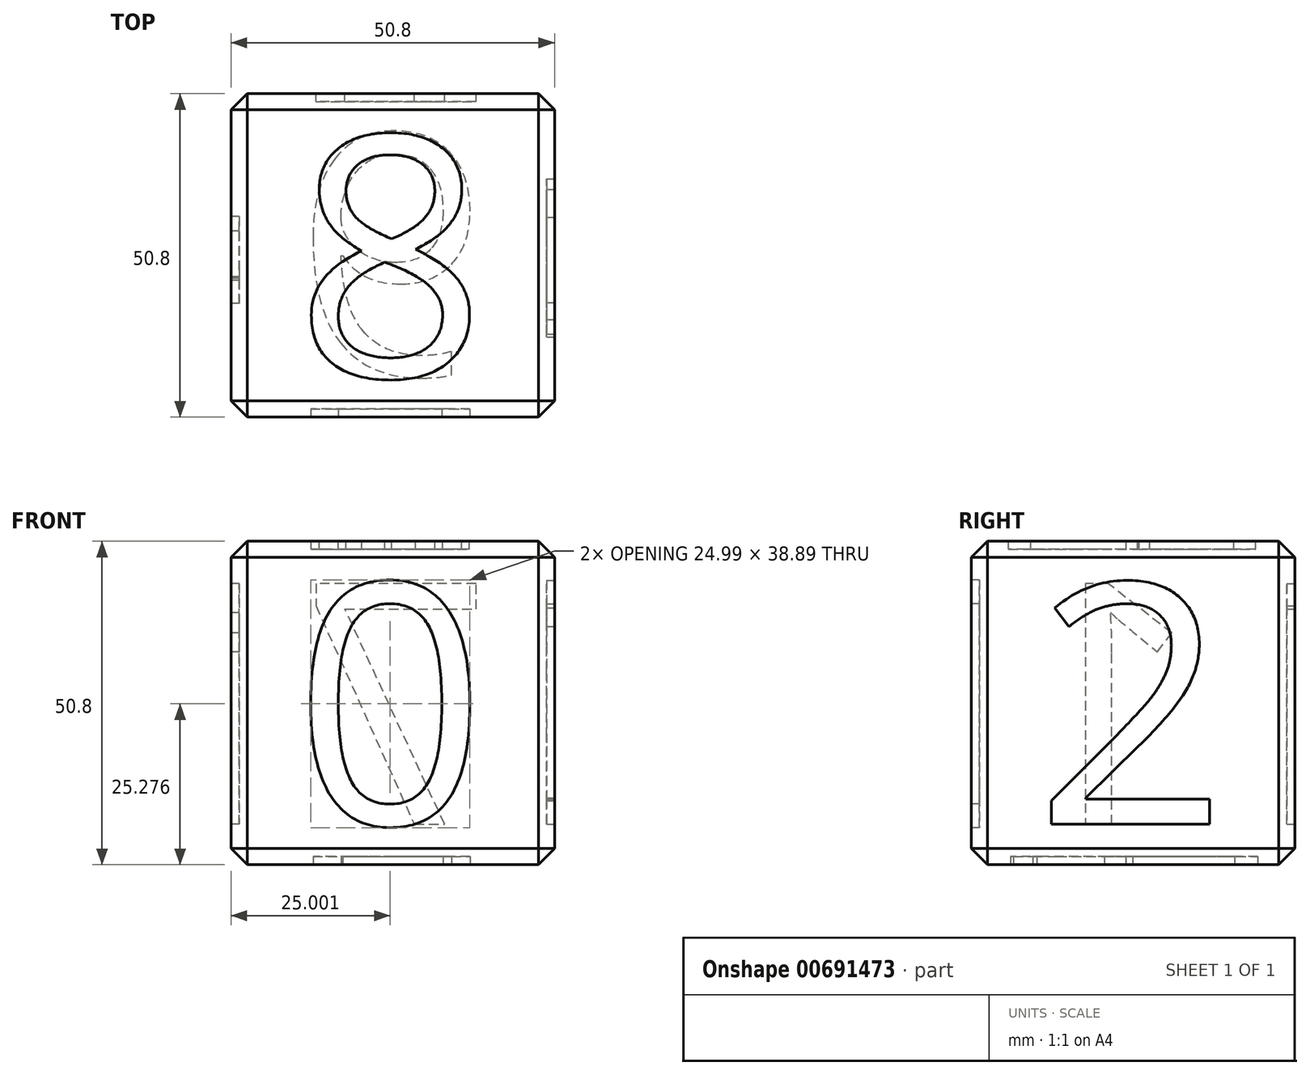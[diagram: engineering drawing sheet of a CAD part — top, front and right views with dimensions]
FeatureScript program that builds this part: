
annotation { "Feature Type Name" : "Feature", "Feature Type Description" : "" }
export const myFeature = defineFeature(function(context is Context, id is Id, definition is map)
    precondition{}
    {
        {
            var Q0;
            Q0=qCreatedBy(makeId("Top.planeOp"),FACE);
            var sketch = newSketch(context, id + "F0", { "sketchPlane" : qUnion([Q0])});
            skLineSegment(sketch, "E0.bottom", {"start": v(25.4, 25.4) * mm, "end": v(-25.4, 25.4) * mm});
            skLineSegment(sketch, "E0.top", {"start": v(25.4, -25.4) * mm, "end": v(-25.4, -25.4) * mm});
            skLineSegment(sketch, "E0.left", {"start": v(25.4, 25.4) * mm, "end": v(25.4, -25.4) * mm});
            skLineSegment(sketch, "E0.right", {"start": v(-25.4, 25.4) * mm, "end": v(-25.4, -25.4) * mm});
            skPoint(sketch, "E0.middle", {"position": v(0, 0) * mm});
            skSolve(sketch);
        }
        {
            var Q0;
            Q0 = qSketchRegion(id + "F0", true);
            extrude(context, id + "F1", {"entities" : qUnion([Q0]), "depth" : 25.4 * mm, "offsetDistance" : 25.4 * mm, "hasSecondDirection" : true, "secondDirectionOppositeDirection" : true, "secondDirectionDepth" : 25.4 * mm});
        }
        {
            var Q0;
            Q0=makeQuery(id+"F1.opExtrude","SWEPT_FACE",FACE,{"disambiguationData":[OSD([sQuery(id+"F0.wireOp",EDGE,"E0.bottom")])]});
            var Q1;
            Q1=makeQuery(id+"F1.opExtrude","CAP_FACE",FACE,{"disambiguationData":[OSD([sQuery(id+"F0.wireOp",EDGE,"E0.bottom"),sQuery(id+"F0.wireOp",EDGE,"E0.top"),sQuery(id+"F0.wireOp",EDGE,"E0.left"),sQuery(id+"F0.wireOp",EDGE,"E0.right")])],"isStart":false});
            var Q2;
            Q2=makeQuery(id+"F1.opExtrude","SWEPT_FACE",FACE,{"disambiguationData":[OSD([sQuery(id+"F0.wireOp",EDGE,"E0.left")])]});
            var Q3;
            Q3=makeQuery(id+"F1.opExtrude","CAP_FACE",FACE,{"disambiguationData":[OSD([sQuery(id+"F0.wireOp",EDGE,"E0.bottom"),sQuery(id+"F0.wireOp",EDGE,"E0.top"),sQuery(id+"F0.wireOp",EDGE,"E0.left"),sQuery(id+"F0.wireOp",EDGE,"E0.right")])],"isStart":true});
            var Q4;
            Q4=makeQuery(id+"F1.opExtrude","SWEPT_FACE",FACE,{"disambiguationData":[OSD([sQuery(id+"F0.wireOp",EDGE,"E0.right")])]});
            var Q5;
            Q5=makeQuery(id+"F1.opExtrude","SWEPT_FACE",FACE,{"disambiguationData":[OSD([sQuery(id+"F0.wireOp",EDGE,"E0.top")])]});
            chamfer(context, id + "F2", {"entities" : qUnion([Q0, Q1, Q2, Q3, Q4, Q5]), "width" : 2.54 * mm, "tangentPropagation" : true});
        }
        {
            var Q0;
            Q0=makeQuery(id+"F1.opExtrude","SWEPT_FACE",FACE,{"disambiguationData":[OSD([sQuery(id+"F0.wireOp",EDGE,"E0.top")])]});
            var sketch = newSketch(context, id + "F3", { "sketchPlane" : qUnion([Q0])});
            skText(sketch, "E1", { "text": "0", "fontName": "OpenSans-Regular.ttf"});
            skLineSegment(sketch, "E2", {"start": v(-29.8, 0) * mm, "end": v(-15.53, 0) * mm, "construction": true});
            const initialGuessF3  = {"E1": [-0.01553, -0.01905, 1, 0, 0.0381]};
            skSetInitialGuess(sketch, initialGuessF3);
            skSolve(sketch);
        }
        {
            var Q0;
            Q0 = qSketchRegion(id + "F3", true);
            extrude(context, id + "F4", {"entities" : qUnion([Q0]), "operationType" : NewBodyOperationType.REMOVE, "oppositeDirection" : true, "depth" : 1.27 * mm, "offsetDistance" : 25.4 * mm});
        }
        {
            var Q0;
            Q0=makeQuery(id+"F1.opExtrude","SWEPT_FACE",FACE,{"disambiguationData":[OSD([sQuery(id+"F0.wireOp",EDGE,"E0.right")])]});
            var sketch = newSketch(context, id + "F5", { "sketchPlane" : qUnion([Q0])});
            skText(sketch, "E3", { "text": "1", "fontName": "OpenSans-Regular.ttf"});
            skLineSegment(sketch, "E4", {"start": v(-10.95, 0) * mm, "end": v(-36.72, 0) * mm, "construction": true});
            const initialGuessF5  = {"E3": [-0.01095, -0.01905, 1, 0, 0.0381]};
            skSetInitialGuess(sketch, initialGuessF5);
            skSolve(sketch);
        }
        {
            var Q0;
            Q0 = qSketchRegion(id + "F5", true);
            extrude(context, id + "F6", {"entities" : qUnion([Q0]), "operationType" : NewBodyOperationType.REMOVE, "oppositeDirection" : true, "depth" : 1.27 * mm, "offsetDistance" : 25.4 * mm});
        }
        {
            var Q0;
            Q0=makeQuery(id+"F1.opExtrude","SWEPT_FACE",FACE,{"disambiguationData":[OSD([sQuery(id+"F0.wireOp",EDGE,"E0.left")])]});
            var sketch = newSketch(context, id + "F7", { "sketchPlane" : qUnion([Q0])});
            skText(sketch, "E5", { "text": "2", "fontName": "OpenSans-Regular.ttf"});
            skLineSegment(sketch, "E6", {"start": v(-15.42, 0) * mm, "end": v(-35.03, 0) * mm, "construction": true});
            const initialGuessF7  = {"E5": [-0.01542, -0.01905, 1, 0, 0.0381]};
            skSetInitialGuess(sketch, initialGuessF7);
            skSolve(sketch);
        }
        {
            var Q0;
            Q0 = qSketchRegion(id + "F7", true);
            extrude(context, id + "F8", {"entities" : qUnion([Q0]), "operationType" : NewBodyOperationType.REMOVE, "oppositeDirection" : true, "depth" : 1.27 * mm, "offsetDistance" : 25.4 * mm});
        }
        {
            var Q0;
            Q0=makeQuery(id+"F1.opExtrude","CAP_FACE",FACE,{"disambiguationData":[OSD([sQuery(id+"F0.wireOp",EDGE,"E0.bottom"),sQuery(id+"F0.wireOp",EDGE,"E0.top"),sQuery(id+"F0.wireOp",EDGE,"E0.left"),sQuery(id+"F0.wireOp",EDGE,"E0.right")])],"isStart":true});
            var sketch = newSketch(context, id + "F9", { "sketchPlane" : qUnion([Q0])});
            skText(sketch, "E7", { "text": "6", "fontName": "OpenSans-Regular.ttf"});
            skLineSegment(sketch, "E8", {"start": v(-15.55, 0) * mm, "end": v(-30.37, 0) * mm, "construction": true});
            const initialGuessF9  = {"E7": [-0.01555, -0.01905, 1, 0, 0.0381]};
            skSetInitialGuess(sketch, initialGuessF9);
            skSolve(sketch);
        }
        {
            var Q0;
            Q0 = qSketchRegion(id + "F9", true);
            extrude(context, id + "F10", {"entities" : qUnion([Q0]), "operationType" : NewBodyOperationType.REMOVE, "oppositeDirection" : true, "depth" : 1.27 * mm, "offsetDistance" : 25.4 * mm});
        }
        {
            var Q0;
            Q0=makeQuery(id+"F1.opExtrude","SWEPT_FACE",FACE,{"disambiguationData":[OSD([sQuery(id+"F0.wireOp",EDGE,"E0.bottom")])]});
            var sketch = newSketch(context, id + "F11", { "sketchPlane" : qUnion([Q0])});
            skText(sketch, "E9", { "text": "7", "fontName": "OpenSans-Regular.ttf"});
            skLineSegment(sketch, "E10", {"start": v(-35.03, 0) * mm, "end": v(-15.5, 0) * mm, "construction": true});
            const initialGuessF11  = {"E9": [-0.0155, -0.01905, 1, 0, 0.0381]};
            skSetInitialGuess(sketch, initialGuessF11);
            skSolve(sketch);
        }
        {
            var Q0;
            Q0 = qSketchRegion(id + "F11", true);
            extrude(context, id + "F12", {"entities" : qUnion([Q0]), "operationType" : NewBodyOperationType.REMOVE, "oppositeDirection" : true, "depth" : 1.27 * mm, "offsetDistance" : 25.4 * mm});
        }
        {
            var Q0;
            Q0=makeQuery(id+"F1.opExtrude","CAP_FACE",FACE,{"disambiguationData":[OSD([sQuery(id+"F0.wireOp",EDGE,"E0.bottom"),sQuery(id+"F0.wireOp",EDGE,"E0.top"),sQuery(id+"F0.wireOp",EDGE,"E0.left"),sQuery(id+"F0.wireOp",EDGE,"E0.right")])],"isStart":false});
            var sketch = newSketch(context, id + "F13", { "sketchPlane" : qUnion([Q0])});
            skText(sketch, "E11", { "text": "8", "fontName": "OpenSans-Regular.ttf"});
            skLineSegment(sketch, "E12", {"start": v(-38.98, 0) * mm, "end": v(-15.47, 0) * mm, "construction": true});
            const initialGuessF13  = {"E11": [-0.01547, -0.01905, 1, 0, 0.0381]};
            skSetInitialGuess(sketch, initialGuessF13);
            skSolve(sketch);
        }
        {
            var Q0;
            Q0 = qSketchRegion(id + "F13", true);
            extrude(context, id + "F14", {"entities" : qUnion([Q0]), "operationType" : NewBodyOperationType.REMOVE, "oppositeDirection" : true, "depth" : 1.27 * mm, "offsetDistance" : 25.4 * mm});
        }
    });
